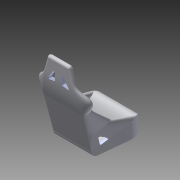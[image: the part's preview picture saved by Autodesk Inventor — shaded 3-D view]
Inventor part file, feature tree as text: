
AUTODESK INVENTOR PART (.ipt)
format: ipt  version: 2015 SP1 (Build 190203100, 203)  size: 1,265,664 bytes
history: native  units: in
note: dims shown in document units (in); Inventor stores cm internally (conversion verified against a paired STEP export)
features: other x2, imported_body x2, revolve x1
ambient origin geometry x8: Origin, YZ Plane, XZ Plane, XY Plane, X Axis, Y Axis, Z Axis, Center Point
bodies: Body1 (feature_tree), Body2 (feature_tree)
feature tree (5):
  revolve  "Revolve7"  [1 undecoded]
  other  "siege1"
  other  "Cut-Extrude11"
  imported_body  "Base1"
  imported_body  "Base2"
note: 1 required parameter value undecoded (feature->parameter linkage not recoverable at this tier; creation-order binding heuristic only, values carry confidence <= 0.55)
